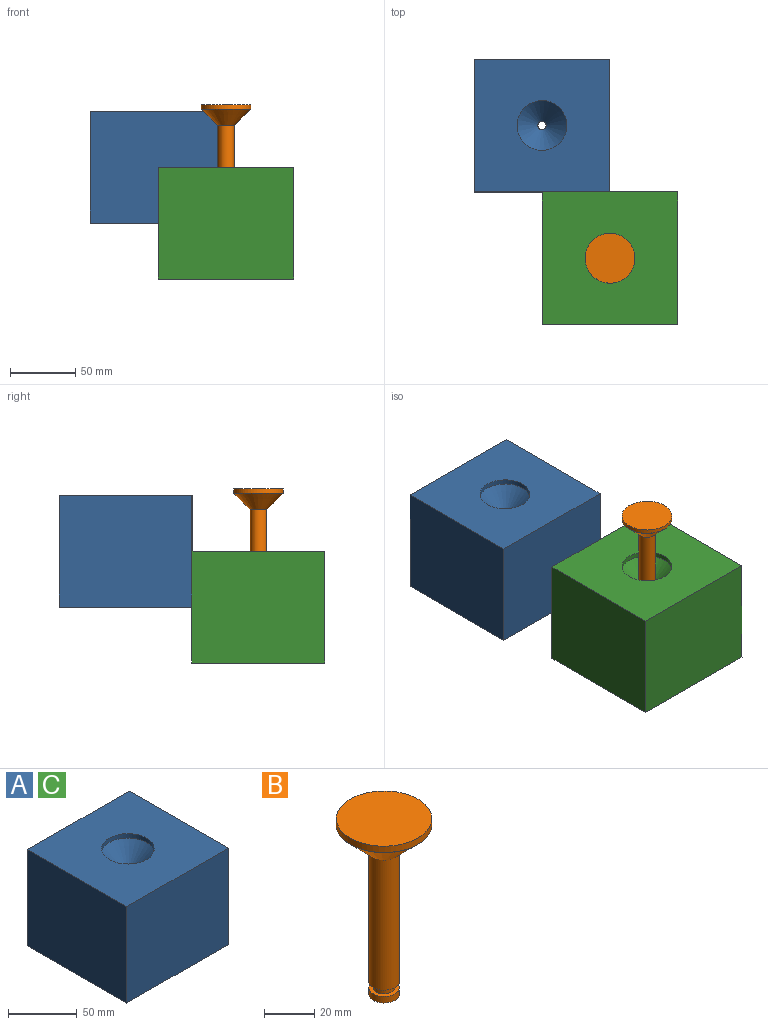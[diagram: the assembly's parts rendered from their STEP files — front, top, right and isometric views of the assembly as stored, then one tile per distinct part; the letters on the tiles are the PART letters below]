
ASSEMBLY  parts=3 mates=2
PART A: 9 faces, bbox 104x101.6x85.6 mm
  f0: plane 104x101.6mm, normal (0,0,1), area 9426.3mm2, adj f1,f3,f4,f5,f6
  f1: plane 101.6x85.56mm, normal (-1,0,0), area 8692.9mm2, adj f0,f2,f4,f5
  f2: plane 104x101.6mm, normal (0,0,-1), area 10534.7mm2, adj f1,f3,f4,f5,f7
  f3: plane 101.6x85.56mm, normal (1,0,0), area 8692.9mm2, adj f0,f2,f4,f5
  f4: plane 104x85.56mm, normal (0,1,0), area 8898.2mm2, adj f0,f1,f2,f3
  f5: plane 104x85.56mm, normal (0,-1,0), area 8898.2mm2, adj f0,f1,f2,f3
  f6: cylinder r=19.05mm len=38.1mm, axis (0,0,1), area 456mm2, adj f0,f8
  f7: cylinder r=3.17mm len=65.88mm, axis (0,0,1), area 1314.1mm2, adj f2,f8
  f8: cone r=3.17mm half-angle=45deg, axis (0,0,1), area 1567.5mm2, adj f6,f7
PART B: 10 faces, bbox 38.1x38.1x85.7 mm
  f0: cylinder r=19.05mm len=38.1mm, axis (0,0,1), area 380mm2, adj f1,f2
  f1: plane 38.1x38.1mm, normal (0,0,-1), area 19.8mm2, adj f0,f3
  f2: plane 38.1x38.1mm, normal (0,0,1), area 1140.1mm2, adj f0
  f3: cone r=6.18mm half-angle=45deg, axis (0,0,1), area 1414.4mm2, adj f1,f4
  f4: cylinder r=6.18mm len=63.5mm, axis (0,0,1), area 2467.2mm2, adj f3,f5
  f5: plane 12.37x12.37mm, normal (0,0,-1), area 62.4mm2, adj f4,f6
  f6: cylinder r=4.29mm len=8.58mm, axis (0,0,1), area 85.5mm2, adj f5,f9
  f7: cylinder r=6.06mm len=12.12mm, axis (0,0,1), area 120.9mm2, adj f8,f9
  f8: plane 12.12x12.12mm, normal (0,0,-1), area 115.4mm2, adj f7
  f9: plane 12.12x12.12mm, normal (0,0,1), area 57.7mm2, adj f6,f7
PART C: same geometry as A
PLACE A rot(axis=(-0.34,0.32,-0.88),0deg) t=(-265.5,221.29,32.11)mm
PLACE B rot(axis=(-0.34,0.32,-0.88),0deg) t=(-342.45,170.49,-18.38)mm
PLACE C rot(axis=(-0.34,0.32,-0.88),0deg) t=(-213.5,119.69,-10.67)mm
MATE cylindrical B.f7 <-> C.f6  axis (0,0,-1) through (-342.45,170.49,-104.1)mm
MATE fastened A.f5 <-> C.f4  axis (0,-1,0) through (-394.45,221.29,-65.95)mm
